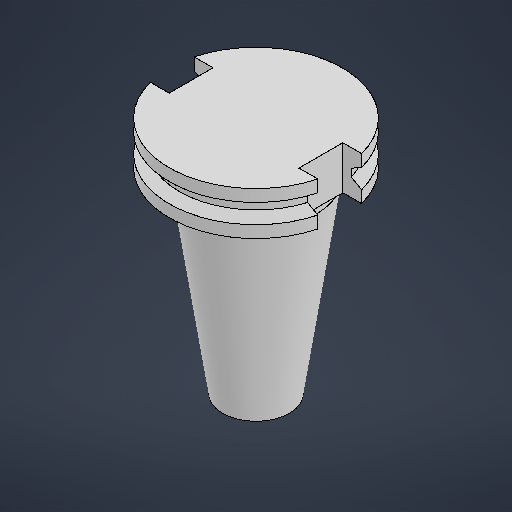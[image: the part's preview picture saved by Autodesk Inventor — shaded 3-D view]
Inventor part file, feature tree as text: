
AUTODESK INVENTOR PART (.ipt)
format: ipt  version: 2025.3 (Build 293356000, 356)  size: 244,224 bytes
history: native  units: mm
features: sketch x2, revolve x1, extrude x1, projected_geometry x1
ambient origin geometry x8: Origin, YZ Plane, XZ Plane, XY Plane, X Axis, Y Axis, Z Axis, Center Point
bodies: Solid1 (feature_tree)
feature tree (5):
  sketch  "Sketch1"  dims[d0=60.0deg d1=56.25mm]
  revolve  "Revolution1"  [1 undecoded]
  extrude  "Extrusion1"  Depth=47.65mm
  sketch  "Sketch2"  dims[d2=63.55mm d3=15.9mm d5=7.0mm d6=72.3mm d7=360.0deg d9=0.0mm d10=0.0mm d12=16.1mm d13=47.65mm d14=3.5mm d15=44.45mm d16=68.4mm d17=1.448623mm d18=25.0mm d19=16.0mm d20=24.493038mm]
  projected_geometry  "Projected Loop1"
note: 1 required parameter value undecoded (feature->parameter linkage not recoverable at this tier; creation-order binding heuristic only, values carry confidence <= 0.55)
